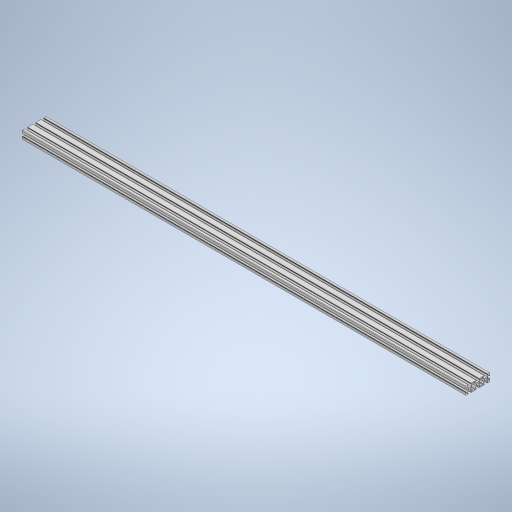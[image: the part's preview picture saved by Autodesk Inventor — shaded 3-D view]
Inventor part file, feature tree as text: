
AUTODESK INVENTOR PART (.ipt)
format: ipt  version: 2023 (Build 270158000, 158)  size: 470,016 bytes
history: native  units: mm
features: mirror x5, extrude x2, sketch x2
ambient origin geometry x8: Origin, YZ Plane, XZ Plane, XY Plane, X Axis, Y Axis, Z Axis, Center Point
bodies: Solid1 (feature_tree)
feature tree (9):
  extrude  "Extrusion1"  Depth=10.0mm
  mirror  "Mirror1"
  mirror  "Mirror2"
  mirror  "Mirror3"
  extrude  "Extrusion2"  Depth=0.5mm
  mirror  "Mirror4"
  mirror  "Mirror5"
  sketch  "Sketch1"  dims[d1=0.5mm d2=10.0mm]
  sketch  "Sketch2"  dims[d3=5.5mm d4=3.7mm d5=2.5mm d8=10.0mm d9=1.5mm d11=6.2mm d12=135.0deg d13=1.5mm d14=1100.0mm d15=0.0mm d16=135.0deg d17=90.0deg d18=0.5mm d19=0.5mm d20=1.0mm d21=1.5mm d22=10.0mm d23=11.0mm d24=7.4mm d25=6.4mm d26=10.0mm d27=1100.0mm d28=0.0mm d29=0.5mm d30=0.872665mm d31=0.5mm d32=0.872665mm]
